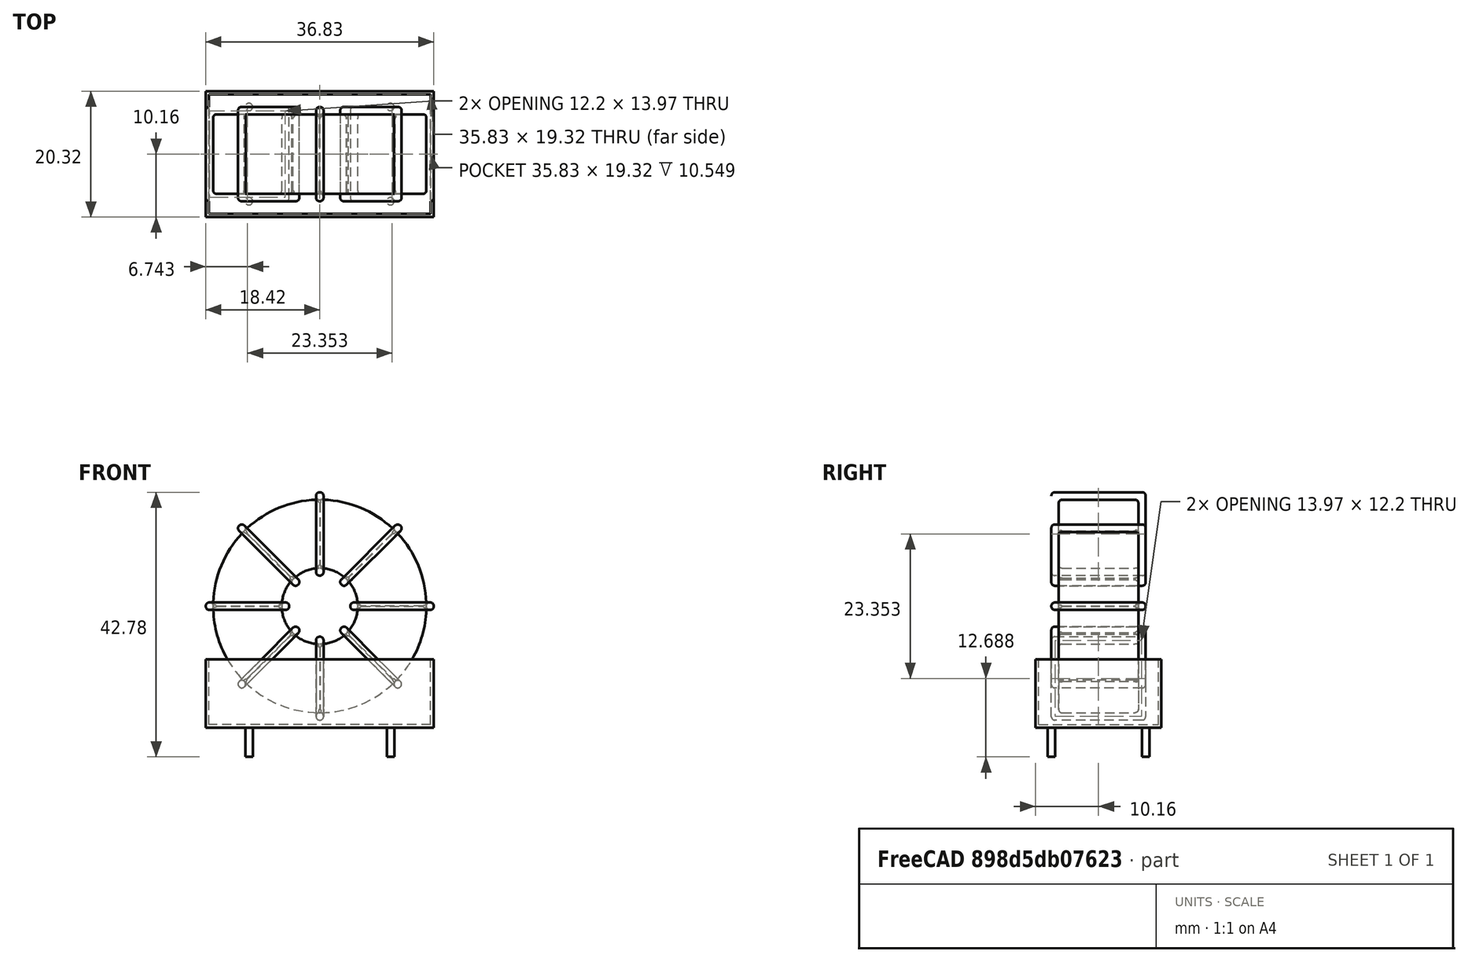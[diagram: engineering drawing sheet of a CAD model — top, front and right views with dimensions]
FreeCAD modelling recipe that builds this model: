
FCSTD DOCUMENT  (FreeCAD 0.16R6712 (Git))
Label: L_CommonMode_Toroid_Vertical_L36.8mm_W20.3mm_Px15.24mm_Py22.86mm_Bourns_8100
License: All rights reserved
LicenseURL: http://en.wikipedia.org/wiki/All_rights_reserved
objects: Sketcher::SketchObject×8, PartDesign::Pad×8, PartDesign::Fillet×5, Spreadsheet::Sheet×1, Part::MultiFuse×1
note: 30 computed .brp shape members not serialized (recipe doc carries the construction recipe); baked Part::Feature solids carry a one-line shape summary decoded from their .brp

FEATURE [Spreadsheet::Sheet] Spreadsheet  label="dimensions"
  cells = A1=Wx; B1(Wx)=36.83; C1(WW)=12.27666666666667; D1(iWx)=36.83; A2=Wy; B2(Wy)=15.24; D2(iWy)=20.32; A3=RM; B3(RMx)=15.24; C3(RMy)=22.86; A4=d_wire; B4(d_wire)=1.2; A5=H; B5(H)=31; A6=offsetx; B6(offsetx)=6.984999999999999
FEATURE [Sketcher::SketchObject] Sketch
  Placement = pos=(11.43,-7.62,0) rot=(1,0,0;1.5708rad)
  expr: Placement.Base.x = Spreadsheet.RMy / 2
  expr: Constraints[4] = Spreadsheet.WW / 2
  expr: Placement.Base.y = -Spreadsheet.RMx / 2
  expr: Constraints[0] = Spreadsheet.Wx / 2 - Spreadsheet.d_wire
  expr: Constraints[2] = Spreadsheet.Wx / 2 + Spreadsheet.d_wire + 0.5
  sketch-geometry (2):
    g0: Circle CenterX=0 CenterY=20.115 CenterZ=0 NormalX=0 NormalY=0 NormalZ=1 Radius=17.215
    g1: Circle CenterX=0 CenterY=20.115 CenterZ=0 NormalX=0 NormalY=0 NormalZ=1 Radius=6.13833
  constraints (5):
    c: Radius(g0) = 17.215
    c: DistanceX(g-1,g0) = 0
    c: DistanceY(g-1,g0) = 20.115
    c: Coincident(g1,g0)
    c: Radius(g1) = 6.13833
FEATURE [PartDesign::Pad] Pad
  Length = 12.84
  Length2 = 100
  Midplane = true
  Placement = pos=(11.43,-7.62,0) rot=(1,0,0;1.5708rad)
  Sketch = -> Sketch
  Type = 0
  expr: Length = Spreadsheet.Wy - 2 * Spreadsheet.d_wire
FEATURE [Sketcher::SketchObject] Sketch001
  Placement = pos=(0,0,0.75) rot=(0,0,1;0rad)
  expr: Constraints[4] = Spreadsheet.RMy
  expr: Constraints[2] = -Spreadsheet.RMx
  expr: Constraints[1] = Spreadsheet.d_wire / 2
  sketch-geometry (4):
    g0: Circle CenterX=0 CenterY=0 CenterZ=0 NormalX=0 NormalY=0 NormalZ=1 Radius=0.6
    g1: Circle CenterX=22.86 CenterY=-15.24 CenterZ=0 NormalX=0 NormalY=0 NormalZ=1 Radius=0.6
    g2: Circle CenterX=0 CenterY=-15.24 CenterZ=0 NormalX=0 NormalY=0 NormalZ=1 Radius=0.6
    g3: Circle CenterX=22.86 CenterY=0 CenterZ=0 NormalX=0 NormalY=0 NormalZ=1 Radius=0.6
  constraints (11):
    c: Equal(g0,g1)
    c: Radius(g0) = 0.6
    c: DistanceY(g-1,g1) = -15.24
    c: Coincident(g0,g-1)
    c: DistanceX(g-1,g1) = 22.86
    c: PointOnObject(g2,g-2)
    c: DistanceY(g-1,g3) = 0
    c: DistanceY(g2,g1) = 0
    c: DistanceX(g3,g1) = 0
    c: Equal(g3,g2)
    c: Equal(g2,g1)
FEATURE [PartDesign::Pad] Pad001
  Length = 5
  Length2 = 0
  Placement = pos=(0,0,0.75) rot=(0,0,1;0rad)
  Reversed = true
  Sketch = -> Sketch001
  Type = 0
FEATURE [PartDesign::Fillet] Fillet
  Base = -> Pad [Edge6,Edge3,Edge2]
  Placement = pos=(11.43,-7.62,0) rot=(1,0,0;1.5708rad)
  Radius = 0.5
FEATURE [Sketcher::SketchObject] Sketch003
  Placement = pos=(11.43,0,20.115) rot=(1,0,0;3.14159rad)
  expr: Placement.Base.x = Spreadsheet.RMy / 2
  expr: Constraints[18] = Spreadsheet.d_wire
  expr: Constraints[16] = Spreadsheet.d_wire
  expr: Constraints[19] = Spreadsheet.d_wire
  expr: Constraints[17] = Spreadsheet.d_wire
  expr: Placement.Base.y = -1 * (Spreadsheet.RMx - Spreadsheet.Wy) / 2
  expr: Constraints[21] = (Spreadsheet.Wx - Spreadsheet.WW) / 2 - Spreadsheet.d_wire
  expr: Constraints[22] = Spreadsheet.Wx / 2 - Spreadsheet.d_wire
  expr: Constraints[43] = Spreadsheet.d_wire
  expr: Constraints[48] = Spreadsheet.Wx - Spreadsheet.d_wire * 2
  expr: Constraints[49] = Spreadsheet.Wy
  expr: Placement.Base.z = Spreadsheet.Wx / 2 + Spreadsheet.d_wire + 0.5
  sketch-geometry (16):
    g0: LineSegment StartX=-4.93833 StartY=0 StartZ=0 EndX=-18.415 EndY=0 EndZ=0
    g1: LineSegment StartX=-18.415 StartY=0 StartZ=0 EndX=-18.415 EndY=15.24 EndZ=0
    g2: LineSegment StartX=-18.415 StartY=15.24 StartZ=0 EndX=-4.93833 EndY=15.24 EndZ=0
    g3: LineSegment StartX=-4.93833 StartY=15.24 StartZ=0 EndX=-4.93833 EndY=0 EndZ=0
    g4: LineSegment StartX=-17.215 StartY=14.04 StartZ=0 EndX=-6.13833 EndY=14.04 EndZ=0
    g5: LineSegment StartX=-6.13833 StartY=14.04 StartZ=0 EndX=-6.13833 EndY=1.2 EndZ=0
    g6: LineSegment StartX=-6.13833 StartY=1.2 StartZ=0 EndX=-17.215 EndY=1.2 EndZ=0
    g7: LineSegment StartX=-17.215 StartY=1.2 StartZ=0 EndX=-17.215 EndY=14.04 EndZ=0
    g8: LineSegment StartX=4.93833 StartY=15.24 StartZ=0 EndX=18.415 EndY=15.24 EndZ=0
    g9: LineSegment StartX=18.415 StartY=15.24 StartZ=0 EndX=18.415 EndY=0 EndZ=0
    g10: LineSegment StartX=18.415 StartY=0 StartZ=0 EndX=4.93833 EndY=0 EndZ=0
    g11: LineSegment StartX=4.93833 StartY=0 StartZ=0 EndX=4.93833 EndY=15.24 EndZ=0
    g12: LineSegment StartX=6.13833 StartY=14.04 StartZ=0 EndX=17.215 EndY=14.04 EndZ=0
    g13: LineSegment StartX=17.215 StartY=14.04 StartZ=0 EndX=17.215 EndY=1.2 EndZ=0
    g14: LineSegment StartX=17.215 StartY=1.2 StartZ=0 EndX=6.13833 EndY=1.2 EndZ=0
    g15: LineSegment StartX=6.13833 StartY=1.2 StartZ=0 EndX=6.13833 EndY=14.04 EndZ=0
  constraints (50):
    c: Horizontal(g0)
    c: Coincident(g1,g0)
    c: Vertical(g1)
    c: Coincident(g2,g1)
    c: Horizontal(g2)
    c: Coincident(g3,g2)
    c: Coincident(g3,g0)
    c: Vertical(g3)
    c: Coincident(g4,g5)
    c: Coincident(g5,g6)
    c: Coincident(g6,g7)
    c: Coincident(g7,g4)
    c: Horizontal(g4)
    c: Horizontal(g6)
    c: Vertical(g5)
    c: Vertical(g7)
    c: DistanceX(g1,g4) = 1.2
    c: DistanceY(g4,g1) = 1.2
    c: DistanceX(g5,g0) = 1.2
    c: DistanceY(g0,g5) = 1.2
    c: DistanceY(g-1,g0) = 0
    c: DistanceX(g6,g6) = 11.0767
    c: DistanceX(g6,g-1) = 17.215
    c: Coincident(g8,g9)
    c: Coincident(g9,g10)
    c: Coincident(g10,g11)
    c: Coincident(g11,g8)
    c: Horizontal(g8)
    c: Horizontal(g10)
    c: Vertical(g9)
    c: Vertical(g11)
    c: Coincident(g12,g13)
    c: Coincident(g13,g14)
    c: Coincident(g14,g15)
    c: Coincident(g15,g12)
    c: Horizontal(g12)
    c: Horizontal(g14)
    c: Vertical(g13)
    c: Vertical(g15)
    c: DistanceY(g8,g2) = 0
    c: DistanceY(g10,g0) = 0
    c: DistanceY(g14,g5) = 0
    c: DistanceY(g12,g4) = 0
    c: DistanceX(g8,g12) = 1.2
    c: Equal(g8,g2)
    c: Equal(g12,g4)
    c: Equal(g9,g1)
    c: Equal(g13,g7)
    c: DistanceX(g4,g12) = 34.43
    c: DistanceY(g0,g1) = 15.24
FEATURE [PartDesign::Pad] Pad002
  Length = 1.2
  Length2 = 100
  Midplane = true
  Placement = pos=(11.43,0,20.115) rot=(1,0,0;3.14159rad)
  Sketch = -> Sketch003
  Type = 0
  expr: Length = Spreadsheet.d_wire
FEATURE [PartDesign::Fillet] Fillet001
  Base = -> Pad002 [Edge38,Edge41,Edge42,Edge43,Edge29,Edge32,Edge33,Edge34,Edge25,Edge35,Edge36,Edge13,Edge14,Edge15,Edge16,Edge17,Edge18,Edge19,Edge1,Edge2,Edge3,Edge4,Edge5,Edge6,Edge7,Edge37,Edge39,Edge40,Edge20,Edge23,Edge24,Edge21,Edge22,Edge8,Edge9,Edge10,Edge11,Edge12,Edge26,Edge27,+8 more]
  Placement = pos=(11.43,0,20.115) rot=(1,0,0;3.14159rad)
  Radius = 0.564
  expr: Radius = Spreadsheet.d_wire * 0.47
FEATURE [Sketcher::SketchObject] Sketch004
  Placement = pos=(11.43,0,20.115) rot=(0.92388,0,0.382683;3.14159rad)
  expr: Placement.Base.x = Spreadsheet.RMy / 2
  expr: Constraints[18] = Spreadsheet.d_wire
  expr: Constraints[16] = Spreadsheet.d_wire
  expr: Constraints[19] = Spreadsheet.d_wire
  expr: Constraints[17] = Spreadsheet.d_wire
  expr: Placement.Base.y = -1 * (Spreadsheet.RMx - Spreadsheet.Wy) / 2
  expr: Constraints[21] = (Spreadsheet.Wx - Spreadsheet.WW) / 2 - Spreadsheet.d_wire
  expr: Constraints[22] = Spreadsheet.Wx / 2 - Spreadsheet.d_wire
  expr: Constraints[43] = Spreadsheet.d_wire
  expr: Constraints[48] = Spreadsheet.Wx - 2 * Spreadsheet.d_wire
  expr: Constraints[49] = Spreadsheet.Wy
  expr: Placement.Base.z = Spreadsheet.Wx / 2 + Spreadsheet.d_wire + 0.5
  sketch-geometry (16):
    g0: LineSegment StartX=-4.93833 StartY=0 StartZ=0 EndX=-18.415 EndY=0 EndZ=0
    g1: LineSegment StartX=-18.415 StartY=0 StartZ=0 EndX=-18.415 EndY=15.24 EndZ=0
    g2: LineSegment StartX=-18.415 StartY=15.24 StartZ=0 EndX=-4.93833 EndY=15.24 EndZ=0
    g3: LineSegment StartX=-4.93833 StartY=15.24 StartZ=0 EndX=-4.93833 EndY=0 EndZ=0
    g4: LineSegment StartX=-17.215 StartY=14.04 StartZ=0 EndX=-6.13833 EndY=14.04 EndZ=0
    g5: LineSegment StartX=-6.13833 StartY=14.04 StartZ=0 EndX=-6.13833 EndY=1.2 EndZ=0
    g6: LineSegment StartX=-6.13833 StartY=1.2 StartZ=0 EndX=-17.215 EndY=1.2 EndZ=0
    g7: LineSegment StartX=-17.215 StartY=1.2 StartZ=0 EndX=-17.215 EndY=14.04 EndZ=0
    g8: LineSegment StartX=4.93833 StartY=15.24 StartZ=0 EndX=18.415 EndY=15.24 EndZ=0
    g9: LineSegment StartX=18.415 StartY=15.24 StartZ=0 EndX=18.415 EndY=0 EndZ=0
    g10: LineSegment StartX=18.415 StartY=0 StartZ=0 EndX=4.93833 EndY=0 EndZ=0
    g11: LineSegment StartX=4.93833 StartY=0 StartZ=0 EndX=4.93833 EndY=15.24 EndZ=0
    g12: LineSegment StartX=6.13833 StartY=14.04 StartZ=0 EndX=17.215 EndY=14.04 EndZ=0
    g13: LineSegment StartX=17.215 StartY=14.04 StartZ=0 EndX=17.215 EndY=1.2 EndZ=0
    g14: LineSegment StartX=17.215 StartY=1.2 StartZ=0 EndX=6.13833 EndY=1.2 EndZ=0
    g15: LineSegment StartX=6.13833 StartY=1.2 StartZ=0 EndX=6.13833 EndY=14.04 EndZ=0
  constraints (50):
    c: Horizontal(g0)
    c: Coincident(g1,g0)
    c: Vertical(g1)
    c: Coincident(g2,g1)
    c: Horizontal(g2)
    c: Coincident(g3,g2)
    c: Coincident(g3,g0)
    c: Vertical(g3)
    c: Coincident(g4,g5)
    c: Coincident(g5,g6)
    c: Coincident(g6,g7)
    c: Coincident(g7,g4)
    c: Horizontal(g4)
    c: Horizontal(g6)
    c: Vertical(g5)
    c: Vertical(g7)
    c: DistanceX(g1,g4) = 1.2
    c: DistanceY(g4,g1) = 1.2
    c: DistanceX(g5,g0) = 1.2
    c: DistanceY(g0,g5) = 1.2
    c: DistanceY(g-1,g0) = 0
    c: DistanceX(g6,g6) = 11.0767
    c: DistanceX(g6,g-1) = 17.215
    c: Coincident(g8,g9)
    c: Coincident(g9,g10)
    c: Coincident(g10,g11)
    c: Coincident(g11,g8)
    c: Horizontal(g8)
    c: Horizontal(g10)
    c: Vertical(g9)
    c: Vertical(g11)
    c: Coincident(g12,g13)
    c: Coincident(g13,g14)
    c: Coincident(g14,g15)
    c: Coincident(g15,g12)
    c: Horizontal(g12)
    c: Horizontal(g14)
    c: Vertical(g13)
    c: Vertical(g15)
    c: DistanceY(g8,g2) = 0
    c: DistanceY(g10,g0) = 0
    c: DistanceY(g14,g5) = 0
    c: DistanceY(g12,g4) = 0
    c: DistanceX(g8,g12) = 1.2
    c: Equal(g8,g2)
    c: Equal(g12,g4)
    c: Equal(g9,g1)
    c: Equal(g13,g7)
    c: DistanceX(g4,g12) = 34.43
    c: DistanceY(g0,g1) = 15.24
FEATURE [PartDesign::Pad] Pad003
  Length = 1.2
  Length2 = 100
  Midplane = true
  Placement = pos=(11.43,0,20.115) rot=(0.92388,0,0.382683;3.14159rad)
  Sketch = -> Sketch004
  Type = 0
  expr: Length = Spreadsheet.d_wire
FEATURE [PartDesign::Fillet] Fillet002
  Base = -> Pad003 [Edge38,Edge41,Edge42,Edge43,Edge29,Edge32,Edge33,Edge34,Edge25,Edge35,Edge36,Edge13,Edge14,Edge15,Edge16,Edge17,Edge18,Edge19,Edge1,Edge2,Edge3,Edge4,Edge5,Edge6,Edge7,Edge37,Edge39,Edge40,Edge20,Edge23,Edge24,Edge21,Edge22,Edge8,Edge9,Edge10,Edge11,Edge12,Edge26,Edge27,+8 more]
  Placement = pos=(11.43,0,20.115) rot=(0.92388,0,0.382683;3.14159rad)
  Radius = 0.564
  expr: Radius = Spreadsheet.d_wire * 0.47
FEATURE [Sketcher::SketchObject] Sketch005
  Placement = pos=(11.43,0,20.115) rot=(0.92388,0,-0.382683;3.14159rad)
  expr: Placement.Base.x = Spreadsheet.RMy / 2
  expr: Constraints[18] = Spreadsheet.d_wire
  expr: Constraints[16] = Spreadsheet.d_wire
  expr: Constraints[19] = Spreadsheet.d_wire
  expr: Constraints[17] = Spreadsheet.d_wire
  expr: Placement.Base.y = -1 * (Spreadsheet.RMx - Spreadsheet.Wy) / 2
  expr: Constraints[21] = (Spreadsheet.Wx - Spreadsheet.WW) / 2 - Spreadsheet.d_wire
  expr: Constraints[22] = Spreadsheet.Wx / 2 - Spreadsheet.d_wire
  expr: Constraints[43] = Spreadsheet.d_wire
  expr: Constraints[48] = Spreadsheet.Wx - 2 * Spreadsheet.d_wire
  expr: Constraints[49] = Spreadsheet.Wy
  expr: Placement.Base.z = Spreadsheet.Wx / 2 + Spreadsheet.d_wire + 0.5
  sketch-geometry (16):
    g0: LineSegment StartX=-4.93833 StartY=0 StartZ=0 EndX=-18.415 EndY=0 EndZ=0
    g1: LineSegment StartX=-18.415 StartY=0 StartZ=0 EndX=-18.415 EndY=15.24 EndZ=0
    g2: LineSegment StartX=-18.415 StartY=15.24 StartZ=0 EndX=-4.93833 EndY=15.24 EndZ=0
    g3: LineSegment StartX=-4.93833 StartY=15.24 StartZ=0 EndX=-4.93833 EndY=0 EndZ=0
    g4: LineSegment StartX=-17.215 StartY=14.04 StartZ=0 EndX=-6.13833 EndY=14.04 EndZ=0
    g5: LineSegment StartX=-6.13833 StartY=14.04 StartZ=0 EndX=-6.13833 EndY=1.2 EndZ=0
    g6: LineSegment StartX=-6.13833 StartY=1.2 StartZ=0 EndX=-17.215 EndY=1.2 EndZ=0
    g7: LineSegment StartX=-17.215 StartY=1.2 StartZ=0 EndX=-17.215 EndY=14.04 EndZ=0
    g8: LineSegment StartX=4.93833 StartY=15.24 StartZ=0 EndX=18.415 EndY=15.24 EndZ=0
    g9: LineSegment StartX=18.415 StartY=15.24 StartZ=0 EndX=18.415 EndY=0 EndZ=0
    g10: LineSegment StartX=18.415 StartY=0 StartZ=0 EndX=4.93833 EndY=0 EndZ=0
    g11: LineSegment StartX=4.93833 StartY=0 StartZ=0 EndX=4.93833 EndY=15.24 EndZ=0
    g12: LineSegment StartX=6.13833 StartY=14.04 StartZ=0 EndX=17.215 EndY=14.04 EndZ=0
    g13: LineSegment StartX=17.215 StartY=14.04 StartZ=0 EndX=17.215 EndY=1.2 EndZ=0
    g14: LineSegment StartX=17.215 StartY=1.2 StartZ=0 EndX=6.13833 EndY=1.2 EndZ=0
    g15: LineSegment StartX=6.13833 StartY=1.2 StartZ=0 EndX=6.13833 EndY=14.04 EndZ=0
  constraints (50):
    c: Horizontal(g0)
    c: Coincident(g1,g0)
    c: Vertical(g1)
    c: Coincident(g2,g1)
    c: Horizontal(g2)
    c: Coincident(g3,g2)
    c: Coincident(g3,g0)
    c: Vertical(g3)
    c: Coincident(g4,g5)
    c: Coincident(g5,g6)
    c: Coincident(g6,g7)
    c: Coincident(g7,g4)
    c: Horizontal(g4)
    c: Horizontal(g6)
    c: Vertical(g5)
    c: Vertical(g7)
    c: DistanceX(g1,g4) = 1.2
    c: DistanceY(g4,g1) = 1.2
    c: DistanceX(g5,g0) = 1.2
    c: DistanceY(g0,g5) = 1.2
    c: DistanceY(g-1,g0) = 0
    c: DistanceX(g6,g6) = 11.0767
    c: DistanceX(g6,g-1) = 17.215
    c: Coincident(g8,g9)
    c: Coincident(g9,g10)
    c: Coincident(g10,g11)
    c: Coincident(g11,g8)
    c: Horizontal(g8)
    c: Horizontal(g10)
    c: Vertical(g9)
    c: Vertical(g11)
    c: Coincident(g12,g13)
    c: Coincident(g13,g14)
    c: Coincident(g14,g15)
    c: Coincident(g15,g12)
    c: Horizontal(g12)
    c: Horizontal(g14)
    c: Vertical(g13)
    c: Vertical(g15)
    c: DistanceY(g8,g2) = 0
    c: DistanceY(g10,g0) = 0
    c: DistanceY(g14,g5) = 0
    c: DistanceY(g12,g4) = 0
    c: DistanceX(g8,g12) = 1.2
    c: Equal(g8,g2)
    c: Equal(g12,g4)
    c: Equal(g9,g1)
    c: Equal(g13,g7)
    c: DistanceX(g4,g12) = 34.43
    c: DistanceY(g0,g1) = 15.24
FEATURE [PartDesign::Pad] Pad004
  Length = 1.2
  Length2 = 100
  Midplane = true
  Placement = pos=(11.43,0,20.115) rot=(0.92388,0,-0.382683;3.14159rad)
  Sketch = -> Sketch005
  Type = 0
  expr: Length = Spreadsheet.d_wire
FEATURE [PartDesign::Fillet] Fillet003
  Base = -> Pad004 [Edge38,Edge41,Edge42,Edge43,Edge29,Edge32,Edge33,Edge34,Edge25,Edge35,Edge36,Edge13,Edge14,Edge15,Edge16,Edge17,Edge18,Edge19,Edge1,Edge2,Edge3,Edge4,Edge5,Edge6,Edge7,Edge37,Edge39,Edge40,Edge20,Edge23,Edge24,Edge21,Edge22,Edge8,Edge9,Edge10,Edge11,Edge12,Edge26,Edge27,+8 more]
  Placement = pos=(11.43,0,20.115) rot=(0.92388,0,-0.382683;3.14159rad)
  Radius = 0.564
  expr: Radius = Spreadsheet.d_wire * 0.47
FEATURE [Sketcher::SketchObject] Sketch006
  Placement = pos=(11.43,0,20.115) rot=(0.707107,0,0.707107;3.14159rad)
  expr: Placement.Base.x = Spreadsheet.RMy / 2
  expr: Constraints[18] = Spreadsheet.d_wire
  expr: Constraints[16] = Spreadsheet.d_wire
  expr: Constraints[19] = Spreadsheet.d_wire
  expr: Constraints[17] = Spreadsheet.d_wire
  expr: Placement.Base.y = -1 * (Spreadsheet.RMx - Spreadsheet.Wy) / 2
  expr: Constraints[21] = (Spreadsheet.Wx - Spreadsheet.WW) / 2 - Spreadsheet.d_wire
  expr: Constraints[22] = Spreadsheet.Wx / 2 - Spreadsheet.d_wire
  expr: Constraints[43] = Spreadsheet.d_wire
  expr: Constraints[48] = Spreadsheet.Wx - Spreadsheet.d_wire * 2
  expr: Constraints[49] = Spreadsheet.Wy
  expr: Placement.Base.z = Spreadsheet.Wx / 2 + Spreadsheet.d_wire + 0.5
  sketch-geometry (16):
    g0: LineSegment StartX=-4.93833 StartY=0 StartZ=0 EndX=-18.415 EndY=0 EndZ=0
    g1: LineSegment StartX=-18.415 StartY=0 StartZ=0 EndX=-18.415 EndY=15.24 EndZ=0
    g2: LineSegment StartX=-18.415 StartY=15.24 StartZ=0 EndX=-4.93833 EndY=15.24 EndZ=0
    g3: LineSegment StartX=-4.93833 StartY=15.24 StartZ=0 EndX=-4.93833 EndY=0 EndZ=0
    g4: LineSegment StartX=-17.215 StartY=14.04 StartZ=0 EndX=-6.13833 EndY=14.04 EndZ=0
    g5: LineSegment StartX=-6.13833 StartY=14.04 StartZ=0 EndX=-6.13833 EndY=1.2 EndZ=0
    g6: LineSegment StartX=-6.13833 StartY=1.2 StartZ=0 EndX=-17.215 EndY=1.2 EndZ=0
    g7: LineSegment StartX=-17.215 StartY=1.2 StartZ=0 EndX=-17.215 EndY=14.04 EndZ=0
    g8: LineSegment StartX=4.93833 StartY=15.24 StartZ=0 EndX=18.415 EndY=15.24 EndZ=0
    g9: LineSegment StartX=18.415 StartY=15.24 StartZ=0 EndX=18.415 EndY=0 EndZ=0
    g10: LineSegment StartX=18.415 StartY=0 StartZ=0 EndX=4.93833 EndY=0 EndZ=0
    g11: LineSegment StartX=4.93833 StartY=0 StartZ=0 EndX=4.93833 EndY=15.24 EndZ=0
    g12: LineSegment StartX=6.13833 StartY=14.04 StartZ=0 EndX=17.215 EndY=14.04 EndZ=0
    g13: LineSegment StartX=17.215 StartY=14.04 StartZ=0 EndX=17.215 EndY=1.2 EndZ=0
    g14: LineSegment StartX=17.215 StartY=1.2 StartZ=0 EndX=6.13833 EndY=1.2 EndZ=0
    g15: LineSegment StartX=6.13833 StartY=1.2 StartZ=0 EndX=6.13833 EndY=14.04 EndZ=0
  constraints (50):
    c: Horizontal(g0)
    c: Coincident(g1,g0)
    c: Vertical(g1)
    c: Coincident(g2,g1)
    c: Horizontal(g2)
    c: Coincident(g3,g2)
    c: Coincident(g3,g0)
    c: Vertical(g3)
    c: Coincident(g4,g5)
    c: Coincident(g5,g6)
    c: Coincident(g6,g7)
    c: Coincident(g7,g4)
    c: Horizontal(g4)
    c: Horizontal(g6)
    c: Vertical(g5)
    c: Vertical(g7)
    c: DistanceX(g1,g4) = 1.2
    c: DistanceY(g4,g1) = 1.2
    c: DistanceX(g5,g0) = 1.2
    c: DistanceY(g0,g5) = 1.2
    c: DistanceY(g-1,g0) = 0
    c: DistanceX(g6,g6) = 11.0767
    c: DistanceX(g6,g-1) = 17.215
    c: Coincident(g8,g9)
    c: Coincident(g9,g10)
    c: Coincident(g10,g11)
    c: Coincident(g11,g8)
    c: Horizontal(g8)
    c: Horizontal(g10)
    c: Vertical(g9)
    c: Vertical(g11)
    c: Coincident(g12,g13)
    c: Coincident(g13,g14)
    c: Coincident(g14,g15)
    c: Coincident(g15,g12)
    c: Horizontal(g12)
    c: Horizontal(g14)
    c: Vertical(g13)
    c: Vertical(g15)
    c: DistanceY(g8,g2) = 0
    c: DistanceY(g10,g0) = 0
    c: DistanceY(g14,g5) = 0
    c: DistanceY(g12,g4) = 0
    c: DistanceX(g8,g12) = 1.2
    c: Equal(g8,g2)
    c: Equal(g12,g4)
    c: Equal(g9,g1)
    c: Equal(g13,g7)
    c: DistanceX(g4,g12) = 34.43
    c: DistanceY(g0,g1) = 15.24
FEATURE [PartDesign::Pad] Pad005
  Length = 1.2
  Length2 = 100
  Midplane = true
  Placement = pos=(11.43,0,20.115) rot=(0.707107,0,0.707107;3.14159rad)
  Sketch = -> Sketch006
  Type = 0
  expr: Length = Spreadsheet.d_wire
FEATURE [PartDesign::Fillet] Fillet004
  Base = -> Pad005 [Edge38,Edge41,Edge42,Edge43,Edge29,Edge32,Edge33,Edge34,Edge25,Edge35,Edge36,Edge13,Edge14,Edge15,Edge16,Edge17,Edge18,Edge19,Edge1,Edge2,Edge3,Edge4,Edge5,Edge6,Edge7,Edge37,Edge39,Edge40,Edge20,Edge23,Edge24,Edge21,Edge22,Edge8,Edge9,Edge10,Edge11,Edge12,Edge26,Edge27,+8 more]
  Placement = pos=(11.43,0,20.115) rot=(0.707107,0,0.707107;3.14159rad)
  Radius = 0.564
  expr: Radius = Spreadsheet.d_wire * 0.47
FEATURE [Sketcher::SketchObject] Sketch007
  Placement = pos=(11.43,0,0.5) rot=(0,0,1;0rad)
  expr: Placement.Base.x = Spreadsheet.RMy / 2
  expr: Placement.Base.z = 0.5
  expr: Constraints[11] = Spreadsheet.iWx / 2
  expr: Constraints[10] = (Spreadsheet.iWy - Spreadsheet.RMx) / 2
  expr: Constraints[9] = Spreadsheet.iWy
  expr: Constraints[8] = Spreadsheet.iWx
  sketch-geometry (4):
    g0: LineSegment StartX=-18.415 StartY=2.54 StartZ=0 EndX=18.415 EndY=2.54 EndZ=0
    g1: LineSegment StartX=18.415 StartY=2.54 StartZ=0 EndX=18.415 EndY=-17.78 EndZ=0
    g2: LineSegment StartX=18.415 StartY=-17.78 StartZ=0 EndX=-18.415 EndY=-17.78 EndZ=0
    g3: LineSegment StartX=-18.415 StartY=-17.78 StartZ=0 EndX=-18.415 EndY=2.54 EndZ=0
  constraints (12):
    c: Coincident(g0,g1)
    c: Coincident(g1,g2)
    c: Coincident(g2,g3)
    c: Coincident(g3,g0)
    c: Horizontal(g0)
    c: Horizontal(g2)
    c: Vertical(g1)
    c: Vertical(g3)
    c: DistanceX(g0,g0) = 36.83
    c: DistanceY(g3,g3) = 20.32
    c: DistanceY(g-1,g0) = 2.54
    c: DistanceX(g0,g-1) = 18.415
FEATURE [PartDesign::Pad] Pad006
  Length = 0.5
  Length2 = 100
  Placement = pos=(11.43,0,0.5) rot=(0,0,1;0rad)
  Sketch = -> Sketch007
  Type = 0
FEATURE [Sketcher::SketchObject] Sketch008
  Placement = pos=(11.43,0,0.5) rot=(0,0,1;0rad)
  expr: Placement.Base.x = Spreadsheet.RMy / 2
  expr: Constraints[8] = Spreadsheet.iWx
  expr: Constraints[9] = Spreadsheet.iWy
  expr: Constraints[10] = (Spreadsheet.iWy - Spreadsheet.RMx) / 2
  expr: Placement.Base.z = 0.5
  expr: Constraints[21] = 0.5
  expr: Constraints[11] = Spreadsheet.iWx / 2
  sketch-geometry (8):
    g0: LineSegment StartX=-18.415 StartY=2.54 StartZ=0 EndX=18.415 EndY=2.54 EndZ=0
    g1: LineSegment StartX=18.415 StartY=2.54 StartZ=0 EndX=18.415 EndY=-17.78 EndZ=0
    g2: LineSegment StartX=18.415 StartY=-17.78 StartZ=0 EndX=-18.415 EndY=-17.78 EndZ=0
    g3: LineSegment StartX=-18.415 StartY=-17.78 StartZ=0 EndX=-18.415 EndY=2.54 EndZ=0
    g4: LineSegment StartX=-17.915 StartY=2.04 StartZ=0 EndX=17.915 EndY=2.04 EndZ=0
    g5: LineSegment StartX=17.915 StartY=2.04 StartZ=0 EndX=17.915 EndY=-17.28 EndZ=0
    g6: LineSegment StartX=17.915 StartY=-17.28 StartZ=0 EndX=-17.915 EndY=-17.28 EndZ=0
    g7: LineSegment StartX=-17.915 StartY=-17.28 StartZ=0 EndX=-17.915 EndY=2.04 EndZ=0
  constraints (24):
    c: Coincident(g0,g1)
    c: Coincident(g1,g2)
    c: Coincident(g2,g3)
    c: Coincident(g3,g0)
    c: Horizontal(g0)
    c: Horizontal(g2)
    c: Vertical(g1)
    c: Vertical(g3)
    c: DistanceX(g0,g0) = 36.83
    c: DistanceY(g3,g3) = 20.32
    c: DistanceY(g-1,g0) = 2.54
    c: DistanceX(g0,g-1) = 18.415
    c: Coincident(g4,g5)
    c: Coincident(g5,g6)
    c: Coincident(g6,g7)
    c: Coincident(g7,g4)
    c: Horizontal(g4)
    c: Horizontal(g6)
    c: Vertical(g5)
    c: Vertical(g7)
    c: DistanceX(g5,g1) = 0.5
    c: DistanceY(g1,g5) = 0.5
    c: DistanceX(g0,g4) = 0.5
    c: DistanceY(g4,g0) = 0.5
FEATURE [PartDesign::Pad] Pad007
  Length = 11.049
  Length2 = 100
  Placement = pos=(11.43,0,0.5) rot=(0,0,1;0rad)
  Sketch = -> Sketch008
  Type = 0
  expr: Length = Spreadsheet.Wx * 0.3
FEATURE [Part::MultiFuse] Pad001_mp_cp  label="L_CommonMode_Toroid_Vertical_L36.8mm_W20.3mm_Px15.24mm_Py22.86mm_Bourns_8100"
  Shapes = -> [Pad001,Fillet,Fillet001,Fillet002,Fillet003,Fillet004,Pad006,Pad007]
